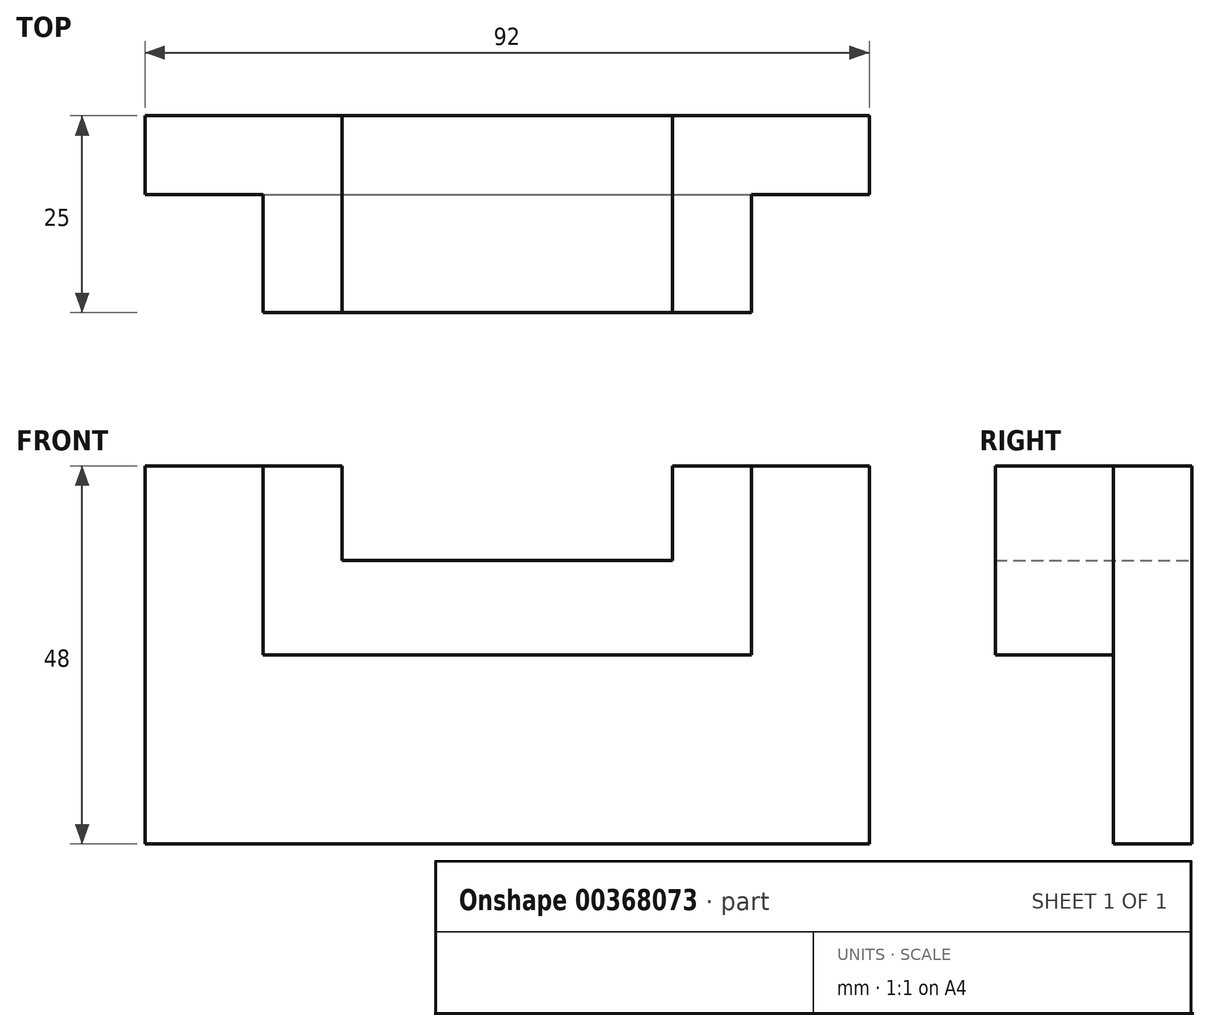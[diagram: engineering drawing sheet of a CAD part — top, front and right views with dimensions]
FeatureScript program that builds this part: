
annotation { "Feature Type Name" : "Feature", "Feature Type Description" : "" }
export const myFeature = defineFeature(function(context is Context, id is Id, definition is map)
    precondition{}
    {
        {
            var Q0;
            Q0=qCreatedBy(makeId("Front.planeOp"),FACE);
            var sketch = newSketch(context, id + "F0", { "sketchPlane" : qUnion([Q0])});
            skLineSegment(sketch, "E0", {"start": v(-46, 24) * mm, "end": v(-46, -24) * mm});
            skLineSegment(sketch, "E1", {"start": v(-46, -24) * mm, "end": v(46, -24) * mm});
            skLineSegment(sketch, "E2", {"start": v(46, -24) * mm, "end": v(46, 24) * mm});
            skLineSegment(sketch, "E3", {"start": v(-46, 24) * mm, "end": v(-31, 24) * mm});
            skLineSegment(sketch, "E4", {"start": v(-31, 24) * mm, "end": v(-31, 0) * mm});
            skLineSegment(sketch, "E5", {"start": v(-31, 0) * mm, "end": v(31, 0) * mm});
            skLineSegment(sketch, "E6", {"start": v(31, 0) * mm, "end": v(31, 24) * mm});
            skLineSegment(sketch, "E7", {"start": v(31, 24) * mm, "end": v(46, 24) * mm});
            skLineSegment(sketch, "E8", {"start": v(-31, 24) * mm, "end": v(-21, 24) * mm});
            skLineSegment(sketch, "E9", {"start": v(-21, 24) * mm, "end": v(-21, 12) * mm});
            skLineSegment(sketch, "E10", {"start": v(-21, 12) * mm, "end": v(21, 12) * mm});
            skLineSegment(sketch, "E11", {"start": v(21, 12) * mm, "end": v(21, 24) * mm});
            skLineSegment(sketch, "E12", {"start": v(21, 24) * mm, "end": v(31, 24) * mm});
            skSolve(sketch);
        }
        {
            var Q0;
            Q0=makeQuery(id+"F0.imprint","IMPRINT",FACE,{"disambiguationData":[TD([[makeQuery(id+"F0.imprint","IMPRINT",EDGE,{"derivedFrom":sQuery(id+"F0.wireOp",EDGE,"E4")}),1.0]])]});
            extrude(context, id + "F1", {"entities" : qUnion([Q0]), "depth" : 25 * mm});
        }
        {
            var Q0;
            Q0=makeQuery(id+"F0.imprint","IMPRINT",FACE,{"disambiguationData":[TD([[makeQuery(id+"F0.imprint","IMPRINT",EDGE,{"derivedFrom":sQuery(id+"F0.wireOp",EDGE,"E0")}),1.0]])]});
            extrude(context, id + "F2", {"entities" : qUnion([Q0]), "operationType" : NewBodyOperationType.ADD, "depth" : 10 * mm});
        }
    });
